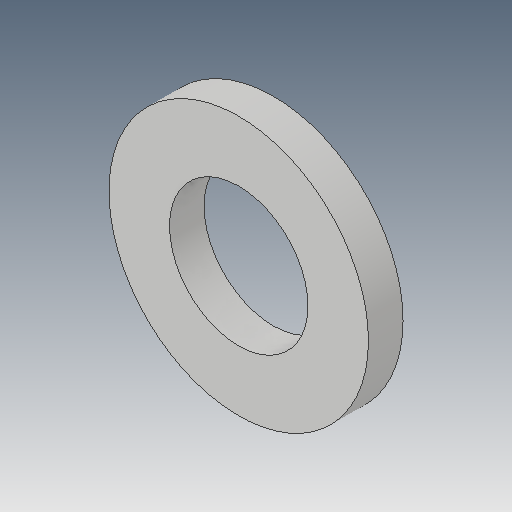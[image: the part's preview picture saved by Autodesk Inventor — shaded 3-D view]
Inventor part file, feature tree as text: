
AUTODESK INVENTOR PART (.ipt)
format: ipt  version: 2017 (Build 210142000, 142)  size: 92,672 bytes
history: native  units: mm
features: other x3, extrude x1, sketch x1, reference x1
ambient origin geometry x8: Origin, YZ Plane, XZ Plane, XY Plane, X Axis, Y Axis, Z Axis, Center Point
bodies: Solid1 (feature_tree)
feature tree (6):
  extrude  "Extrusion1"  Depth=0.8mm
  sketch  "Sketch1"  dims[d0=3.2mm d1=6.0mm d2=0.8mm d3=0.0mm]
  reference  "Reference1"
  other  "<userpath>\OneDrive\SL-Inventor\SL-Beast 3D Printer\x-aXIS-aSSEMBLY.iam"
  other  "x-aXIS-aSSEMBLY.iam"
  other  "M1173041- NEMA 17:1"
